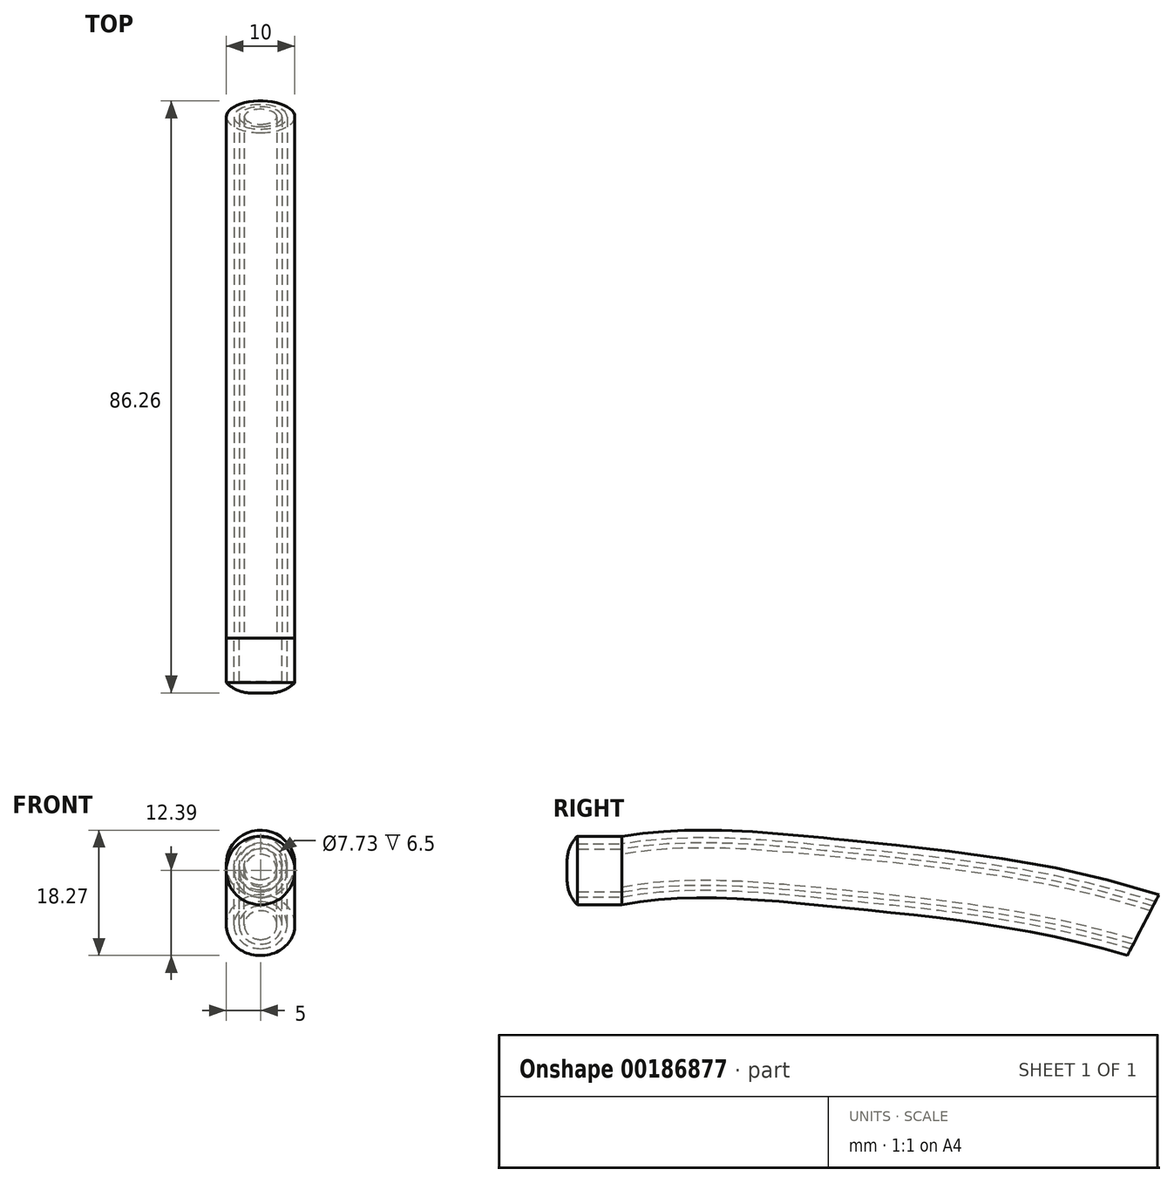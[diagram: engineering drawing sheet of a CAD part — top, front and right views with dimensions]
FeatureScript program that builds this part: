
annotation { "Feature Type Name" : "Feature", "Feature Type Description" : "" }
export const myFeature = defineFeature(function(context is Context, id is Id, definition is map)
    precondition{}
    {
        {
            var Q0;
            Q0=qCreatedBy(makeId("Front.planeOp"),FACE);
            var sketch = newSketch(context, id + "F0", { "sketchPlane" : qUnion([Q0])});
            skCircle(sketch, "E0", {"center": v(0, 0) * mm, "radius": 5 * mm});
            skCircle(sketch, "E1", {"center": v(0, 0) * mm, "radius": 3.87 * mm});
            skSolve(sketch);
        }
        {
            var Q0;
            Q0=qCreatedBy(makeId("Right.planeOp"),FACE);
            var sketch = newSketch(context, id + "F1", { "sketchPlane" : qUnion([Q0])});
            skFitSpline(sketch, "E2", {"points": [v(0, 0) * mm, v(32.86, -0.53) * mm, v(75.95, -7.96) * mm], "startDerivative": vector(65.78, 11.9) * mm, "endDerivative": vector(85.48, -26.55) * mm});
            skSolve(sketch);
        }
        {
            var Q0;
            Q0 = qSketchRegion(id + "F0", true);
            var Q1;
            Q1 = qConstructionFilter(qBodyType(qCreatedBy(id + "F1" ,EDGE), BodyType.WIRE), ConstructionObject.NO);
            sweep(context, id + "F2", {"profiles" : qUnion([Q0]), "path" : qUnion([Q1])});
        }
        {
            var Q0;
            Q0 = qSketchRegion(id + "F0", true);
            extrude(context, id + "F3", {"entities" : qUnion([Q0]), "depth" : 6.5 * mm});
        }
        {
            var Q0;
            Q0=qCreatedBy(makeId("Front.planeOp"),FACE);
            var sketch = newSketch(context, id + "F4", { "sketchPlane" : qUnion([Q0])});
            skCircle(sketch, "E3", {"center": v(0, 0) * mm, "radius": 3.12 * mm});
            skSolve(sketch);
        }
        {
            var Q0;
            Q0=makeQuery(id+"F4.imprint","IMPRINT",FACE,{"disambiguationData":[TD([[makeQuery(id+"F4.imprint","IMPRINT",EDGE,{"derivedFrom":sQuery(id+"F4.wireOp",EDGE,"E3")}),1.0]])]});
            extrude(context, id + "F5", {"entities" : qUnion([Q0]), "depth" : 6.35 * mm});
        }
        {
            var Q0;
            Q0=qCreatedBy(makeId("Front.planeOp"),FACE);
            cPlane(context, id + "F6", {"entities" : qUnion([Q0]), "cplaneType" : CPlaneType.OFFSET, "offset" : 6.5 * mm, "width" : 152.4 * mm, "height" : 152.4 * mm});
        }
        {
            var Q0;
            Q0=qCreatedBy(id+"F6.planeOp",FACE);
            var sketch = newSketch(context, id + "F7", { "sketchPlane" : qUnion([Q0])});
            skCircle(sketch, "E4", {"center": v(0, 0) * mm, "radius": 5 * mm});
            skSolve(sketch);
        }
        {
            var Q0;
            Q0 = qSketchRegion(id + "F7", true);
            extrude(context, id + "F8", {"entities" : qUnion([Q0]), "depth" : 1.5 * mm});
        }
        {
            var Q0;
            Q0=makeQuery(id+"F8.opExtrude","CAP_FACE",FACE,{"disambiguationData":[OSD([sQuery(id+"F7.wireOp",EDGE,"E4")])],"isStart":false});
            fillet(context, id + "F9", {"entities" : qUnion([Q0]), "radius" : 5 * mm, "tangentPropagation" : true, "allowEdgeOverflow" : false});
        }
        {
            var Q0;
            Q0=qCreatedBy(makeId("Front.planeOp"),FACE);
            var sketch = newSketch(context, id + "F10", { "sketchPlane" : qUnion([Q0])});
            skCircle(sketch, "E5", {"center": v(0, 0) * mm, "radius": 2.37 * mm});
            skSolve(sketch);
        }
        {
            var Q0;
            Q0=makeQuery(id+"F5.opExtrude","CAP_FACE",FACE,{"disambiguationData":[OSD([sQuery(id+"F4.wireOp",EDGE,"E3")])],"isStart":true});
            var Q1;
            Q1 = qConstructionFilter(qBodyType(qCreatedBy(id + "F1" ,EDGE), BodyType.WIRE), ConstructionObject.NO);
            sweep(context, id + "F11", {"profiles" : qUnion([Q0]), "path" : qUnion([Q1])});
        }
        {
            var Q0;
            Q0 = qSketchRegion(id + "F10", true);
            var Q1;
            Q1 = qConstructionFilter(qBodyType(qCreatedBy(id + "F1" ,EDGE), BodyType.WIRE), ConstructionObject.NO);
            sweep(context, id + "F12", {"operationType" : NewBodyOperationType.REMOVE, "profiles" : qUnion([Q0]), "path" : qUnion([Q1])});
        }
    });
